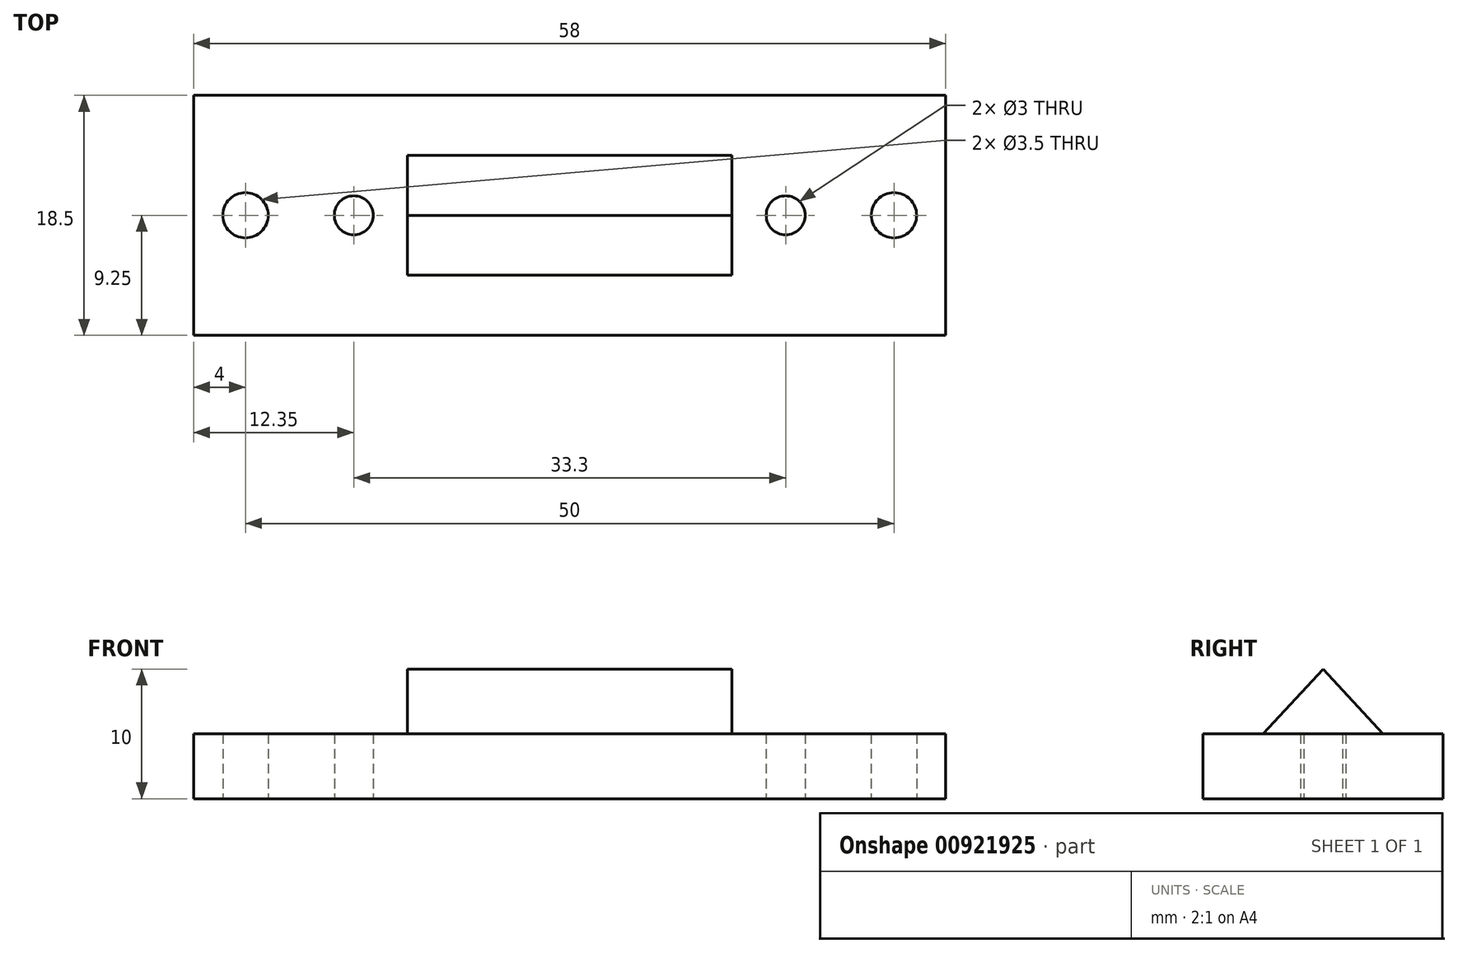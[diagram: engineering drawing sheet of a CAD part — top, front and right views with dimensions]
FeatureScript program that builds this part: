
annotation { "Feature Type Name" : "Feature", "Feature Type Description" : "" }
export const myFeature = defineFeature(function(context is Context, id is Id, definition is map)
    precondition{}
    {
        {
            var Q0;
            Q0=qCreatedBy(makeId("Top.planeOp"),FACE);
            var sketch = newSketch(context, id + "F0", { "sketchPlane" : qUnion([Q0])});
            skLineSegment(sketch, "E0.bottom", {"start": v(19, -9.25) * mm, "end": v(-19, -9.25) * mm});
            skLineSegment(sketch, "E0.top", {"start": v(19, 9.25) * mm, "end": v(-19, 9.25) * mm});
            skLineSegment(sketch, "E0.left", {"start": v(19, -9.25) * mm, "end": v(19, 9.25) * mm});
            skLineSegment(sketch, "E0.right", {"start": v(-19, -9.25) * mm, "end": v(-19, 9.25) * mm});
            skPoint(sketch, "E0.middle", {"position": v(0, 0) * mm});
            skLineSegment(sketch, "E1.bottom", {"start": v(19, -9.25) * mm, "end": v(29, -9.25) * mm});
            skLineSegment(sketch, "E1.top", {"start": v(19, 9.25) * mm, "end": v(29, 9.25) * mm});
            skLineSegment(sketch, "E1.right", {"start": v(29, -9.25) * mm, "end": v(29, 9.25) * mm});
            skLineSegment(sketch, "E2.bottom", {"start": v(-19, -9.25) * mm, "end": v(-29, -9.25) * mm});
            skLineSegment(sketch, "E2.top", {"start": v(-19, 9.25) * mm, "end": v(-29, 9.25) * mm});
            skLineSegment(sketch, "E2.right", {"start": v(-29, -9.25) * mm, "end": v(-29, 9.25) * mm});
            skCircle(sketch, "E3", {"center": v(-25, 0) * mm, "radius": 1.75 * mm});
            skPoint(sketch, "E3.centerSnap0", {"position": v(-29, 0) * mm});
            skCircle(sketch, "E4", {"center": v(25, 0) * mm, "radius": 1.75 * mm});
            skPoint(sketch, "E4.centerSnap0", {"position": v(29, 0) * mm});
            skCircle(sketch, "E5", {"center": v(-16.65, 0) * mm, "radius": 1.5 * mm});
            skCircle(sketch, "E6", {"center": v(16.65, 0) * mm, "radius": 1.5 * mm});
            skSolve(sketch);
        }
        {
            var Q0;
            Q0=qSketchRegion(id+"F0",true);
            extrude(context, id + "F1", {"entities" : qUnion([Q0]), "depth" : 5 * mm, "offsetDistance" : 25 * mm});
        }
        {
            var Q0;
            Q0=makeQuery(id+"F1.opExtrude","CAP_FACE",FACE,{"disambiguationData":[OSD([sQuery(id+"F0.wireOp",EDGE,"E0.bottom"),sQuery(id+"F0.wireOp",EDGE,"E0.top"),sQuery(id+"F0.wireOp",EDGE,"E1.bottom"),sQuery(id+"F0.wireOp",EDGE,"E1.top"),sQuery(id+"F0.wireOp",EDGE,"E1.right"),sQuery(id+"F0.wireOp",EDGE,"E2.bottom"),sQuery(id+"F0.wireOp",EDGE,"E2.top"),sQuery(id+"F0.wireOp",EDGE,"E2.right"),sQuery(id+"F0.wireOp",EDGE,"E3"),sQuery(id+"F0.wireOp",EDGE,"E4"),sQuery(id+"F0.wireOp",EDGE,"E5"),sQuery(id+"F0.wireOp",EDGE,"E6")])],"isStart":false});
            var sketch = newSketch(context, id + "F2", { "sketchPlane" : qUnion([Q0])});
            skLineSegment(sketch, "E7.bottom", {"start": v(12.5, 9.25) * mm, "end": v(-12.5, 9.25) * mm});
            skLineSegment(sketch, "E7.top", {"start": v(12.5, -9.25) * mm, "end": v(-12.5, -9.25) * mm});
            skLineSegment(sketch, "E7.left", {"start": v(12.5, 9.25) * mm, "end": v(12.5, -9.25) * mm});
            skLineSegment(sketch, "E7.right", {"start": v(-12.5, 9.25) * mm, "end": v(-12.5, -9.25) * mm});
            skPoint(sketch, "E7.middle", {"position": v(0, 0) * mm});
            skSolve(sketch);
        }
        {
            var Q0;
            Q0=qSketchRegion(id+"F2",true);
            extrude(context, id + "F3", {"entities" : qUnion([Q0]), "operationType" : NewBodyOperationType.ADD, "depth" : 5 * mm, "offsetDistance" : 25 * mm});
        }
        {
            var Q0;
            Q0=makeQuery(id+"F3.opExtrude","SWEPT_FACE",FACE,{"disambiguationData":[OSD([sQuery(id+"F2.wireOp",EDGE,"E7.right")])]});
            var sketch = newSketch(context, id + "F4", { "sketchPlane" : qUnion([Q0])});
            skLineSegment(sketch, "E8", {"start": v(0, 10) * mm, "end": v(9.25, 0) * mm});
            skLineSegment(sketch, "E9", {"start": v(0, 10) * mm, "end": v(-9.25, 0) * mm});
            skLineSegment(sketch, "E10", {"start": v(-9.25, 0) * mm, "end": v(9.25, 0) * mm});
            skLineSegment(sketch, "E11", {"start": v(-9.25, 0) * mm, "end": v(-9.25, 10) * mm});
            skLineSegment(sketch, "E12", {"start": v(-9.25, 10) * mm, "end": v(0, 10) * mm});
            skLineSegment(sketch, "E13", {"start": v(0, 10) * mm, "end": v(9.25, 10) * mm});
            skLineSegment(sketch, "E14", {"start": v(9.25, 10) * mm, "end": v(9.25, 0) * mm});
            skSolve(sketch);
        }
        {
            var Q0;
            {var subQ0=sQuery(id+"F4.wireOp",EDGE,"E12");Q0=makeQuery(id+"F4.imprint","IMPRINT",FACE,{"disambiguationData":[TD([[makeQuery(id+"F4.imprint","IMPRINT",EDGE,{"derivedFrom":subQ0}),-1.0]])]});}
            var Q1;
            {var subQ0=sQuery(id+"F4.wireOp",EDGE,"E13");Q1=makeQuery(id+"F4.imprint","IMPRINT",FACE,{"disambiguationData":[TD([[makeQuery(id+"F4.imprint","IMPRINT",EDGE,{"derivedFrom":subQ0}),-1.0]])]});}
            var Q2;
            {var subQ0=sQuery(id+"F4.wireOp",EDGE,"E14");var subQ3=makeQuery(id+"F3.opExtrude","CAP_EDGE",EDGE,{"disambiguationData":[OSD([sQuery(id+"F2.wireOp",EDGE,"E7.right")])],"isStart":true});var subQ5=makeQuery(id+"F4.imprint","INTERSECT",VERTEX,{"derivedFrom":[subQ3,subQ0]});Q2=makeQuery(id+"F4.imprint","IMPRINT",FACE,{"disambiguationData":[TD([[makeQuery(id+"F4.imprint","IMPRINT",EDGE,{"disambiguationData":[TD([[subQ5,1.0]])],"derivedFrom":subQ3}),-1.0]])]});}
            var Q3;
            {var subQ0=sQuery(id+"F4.wireOp",EDGE,"E11");var subQ3=makeQuery(id+"F3.opExtrude","CAP_EDGE",EDGE,{"disambiguationData":[OSD([sQuery(id+"F2.wireOp",EDGE,"E7.right")])],"isStart":true});var subQ5=makeQuery(id+"F4.imprint","INTERSECT",VERTEX,{"derivedFrom":[subQ3,subQ0]});Q3=makeQuery(id+"F4.imprint","IMPRINT",FACE,{"disambiguationData":[TD([[makeQuery(id+"F4.imprint","IMPRINT",EDGE,{"disambiguationData":[TD([[subQ5,-1.0]])],"derivedFrom":subQ3}),-1.0]])]});}
            extrude(context, id + "F5", {"entities" : qUnion([Q0, Q1, Q2, Q3]), "operationType" : NewBodyOperationType.REMOVE, "endBound" : BoundingType.THROUGH_ALL, "oppositeDirection" : true, "depth" : 25 * mm, "offsetDistance" : 25 * mm, "hasSecondDirection" : true, "secondDirectionBound" : SecondDirectionBoundingType.THROUGH_ALL, "secondDirectionOppositeDirection" : false, "secondDirectionDepth" : 25 * mm});
        }
    });
